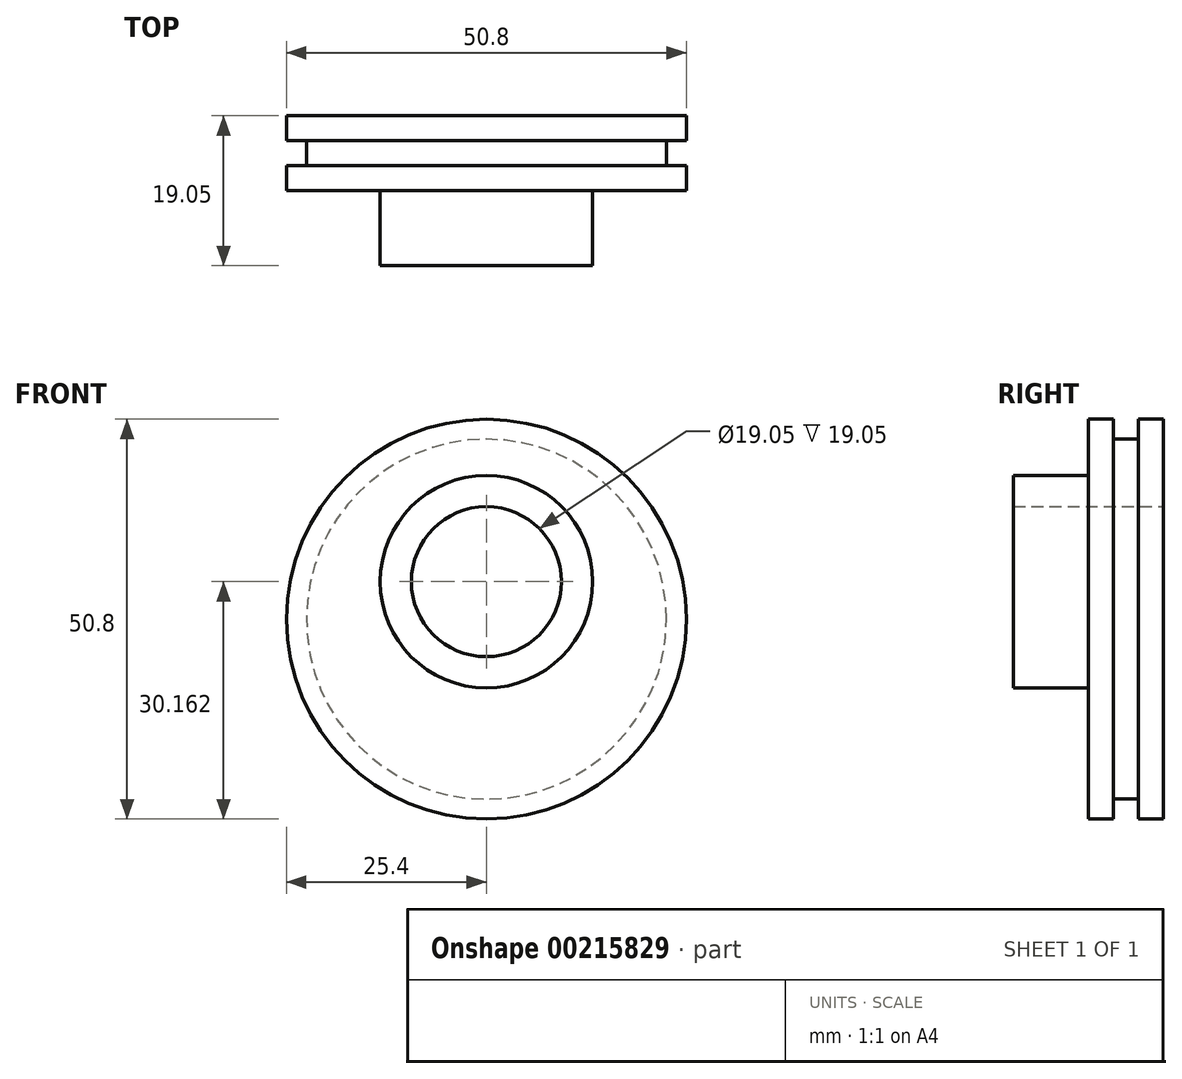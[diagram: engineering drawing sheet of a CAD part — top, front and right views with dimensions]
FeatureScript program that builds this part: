
annotation { "Feature Type Name" : "Feature", "Feature Type Description" : "" }
export const myFeature = defineFeature(function(context is Context, id is Id, definition is map)
    precondition{}
    {
        {
            var Q0;
            Q0=qCreatedBy(makeId("Front.planeOp"),FACE);
            var sketch = newSketch(context, id + "F0", { "sketchPlane" : qUnion([Q0])});
            skCircle(sketch, "E0", {"center": v(0, 0) * mm, "radius": 25.4 * mm});
            skSolve(sketch);
        }
        {
            var Q0;
            Q0=qSketchRegion(id+"F0",true);
            extrude(context, id + "F1", {"entities" : qUnion([Q0]), "endBound" : BoundingType.SYMMETRIC, "depth" : 9.52 * mm});
        }
        {
            var Q0;
            Q0=makeQuery(id+"F1.opExtrude","CAP_FACE",FACE,{"disambiguationData":[OSD([sQuery(id+"F0.wireOp",EDGE,"E0")])],"isStart":true});
            var sketch = newSketch(context, id + "F2", { "sketchPlane" : qUnion([Q0])});
            skCircle(sketch, "E1", {"center": v(0, 4.76) * mm, "radius": 9.53 * mm});
            skSolve(sketch);
        }
        {
            var Q0;
            Q0=qSketchRegion(id+"F2",true);
            var Q1;
            Q1=qConstructionFilter(qBodyType(qCreatedBy(id+"F2",EDGE),BodyType.WIRE),ConstructionObject.NO);
            extrude(context, id + "F3", {"entities" : qUnion([Q0]), "operationType" : NewBodyOperationType.REMOVE, "surfaceEntities" : qUnion([Q1]), "endBound" : BoundingType.UP_TO_NEXT, "oppositeDirection" : true, "depth" : 25.4 * mm});
        }
        {
            var Q0;
            Q0=makeQuery(id+"F1.opExtrude","CAP_FACE",FACE,{"disambiguationData":[OSD([sQuery(id+"F0.wireOp",EDGE,"E0")])],"isStart":false});
            var sketch = newSketch(context, id + "F4", { "sketchPlane" : qUnion([Q0])});
            skCircle(sketch, "E2", {"center": v(0, 4.76) * mm, "radius": 13.5 * mm});
            skSolve(sketch);
        }
        {
            var Q0;
            Q0=makeQuery(id+"F4.imprint","IMPRINT",FACE,{"disambiguationData":[TD([[makeQuery(id+"F4.imprint","IMPRINT",EDGE,{"derivedFrom":sQuery(id+"F4.wireOp",EDGE,"E2")}),1.0]])]});
            extrude(context, id + "F5", {"entities" : qUnion([Q0]), "operationType" : NewBodyOperationType.ADD, "depth" : 9.52 * mm});
        }
        {
            var Q0;
            Q0=qCreatedBy(makeId("Front.planeOp"),FACE);
            var sketch = newSketch(context, id + "F6", { "sketchPlane" : qUnion([Q0])});
            skCircle(sketch, "E3.0", {"center": v(0, 0) * mm, "radius": 25.4 * mm});
            skCircle(sketch, "E4.0", {"center": v(0, 0) * mm, "radius": 22.86 * mm});
            skSolve(sketch);
        }
        {
            var Q0;
            Q0=qSketchRegion(id+"F6",true);
            extrude(context, id + "F7", {"entities" : qUnion([Q0]), "operationType" : NewBodyOperationType.REMOVE, "endBound" : BoundingType.SYMMETRIC, "depth" : 3.17 * mm});
        }
    });
